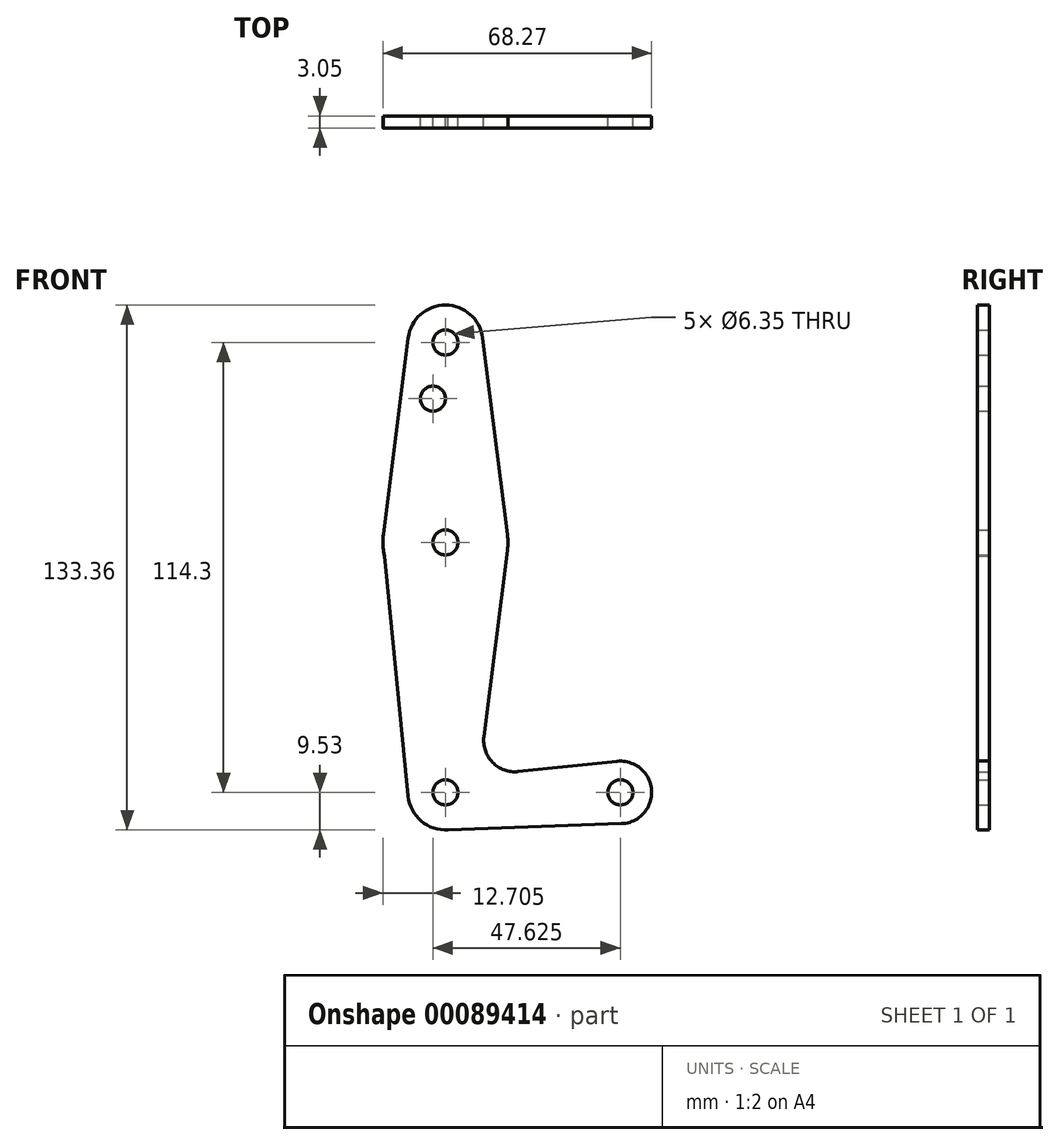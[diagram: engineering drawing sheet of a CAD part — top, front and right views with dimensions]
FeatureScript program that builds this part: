
annotation { "Feature Type Name" : "Feature", "Feature Type Description" : "" }
export const myFeature = defineFeature(function(context is Context, id is Id, definition is map)
    precondition{}
    {
        {
            var Q0;
            Q0=qCreatedBy(makeId("Front.planeOp"),FACE);
            var sketch = newSketch(context, id + "F0", { "sketchPlane" : qUnion([Q0])});
            skLineSegment(sketch, "E0", {"start": v(0, 114.3) * mm, "end": v(0, 0) * mm});
            skLineSegment(sketch, "E1", {"start": v(0, 0) * mm, "end": v(44.45, 0) * mm});
            skCircle(sketch, "E2", {"center": v(0, 114.3) * mm, "radius": 9.53 * mm});
            skCircle(sketch, "E3", {"center": v(0, 63.5) * mm, "radius": 15.88 * mm});
            skCircle(sketch, "E4", {"center": v(0, 0) * mm, "radius": 9.53 * mm});
            skCircle(sketch, "E5", {"center": v(44.45, 0) * mm, "radius": 7.94 * mm});
            skLineSegment(sketch, "E6", {"start": v(0, -9.53) * mm, "end": v(44.73, -7.93) * mm});
            skCircle(sketch, "E7", {"center": v(0, 114.3) * mm, "radius": 3.18 * mm});
            skCircle(sketch, "E8", {"center": v(-3.18, 100.03) * mm, "radius": 3.18 * mm});
            skCircle(sketch, "E9", {"center": v(0, 63.5) * mm, "radius": 3.18 * mm});
            skCircle(sketch, "E10", {"center": v(0, 0) * mm, "radius": 3.18 * mm});
            skCircle(sketch, "E11", {"center": v(44.45, 0) * mm, "radius": 3.18 * mm});
            skLineSegment(sketch, "E12", {"start": v(-9.45, 115.5) * mm, "end": v(-15.75, 65.48) * mm});
            skLineSegment(sketch, "E13", {"start": v(9.45, 115.5) * mm, "end": v(15.75, 65.48) * mm});
            skLineSegment(sketch, "E14", {"start": v(15.75, 61.52) * mm, "end": v(9.79, 14.17) * mm});
            skLineSegment(sketch, "E15", {"start": v(18.5, 5.27) * mm, "end": v(43.63, 7.9) * mm});
            skPoint(sketch, "E16.visualSharp", {"position": v(8.53, 4.23) * mm});
            skArc(sketch, "E16.filletArc", {"start": v(9.79, 14.17) * mm, "mid": v(12, 7.62) * mm, "end": v(18.5, 5.27) * mm});
            skLineSegment(sketch, "E17", {"start": v(-15.5, 60.09) * mm, "end": v(-9.48, -0.94) * mm});
            skSolve(sketch);
        }
        {
            var Q0;
            Q0 = qSketchRegion(id + "F0", true);
            var Q1;
            {var subQ0=sQuery(id+"F0.wireOp",EDGE,"E4");var subQ1=sQuery(id+"F0.wireOp",EDGE,"E0");var subQ2=makeQuery(id+"F0.imprint","INTERSECT",VERTEX,{"derivedFrom":[subQ1,subQ0]});Q1=makeQuery(id+"F0.imprint","IMPRINT",FACE,{"disambiguationData":[TD([[makeQuery(id+"F0.imprint","IMPRINT",EDGE,{"disambiguationData":[TD([[subQ2,-1.0]])],"derivedFrom":subQ1}),1.0]])]});}
            extrude(context, id + "F1", {"entities" : qUnion([Q0, Q1]), "depth" : 3.05 * mm});
        }
    });
